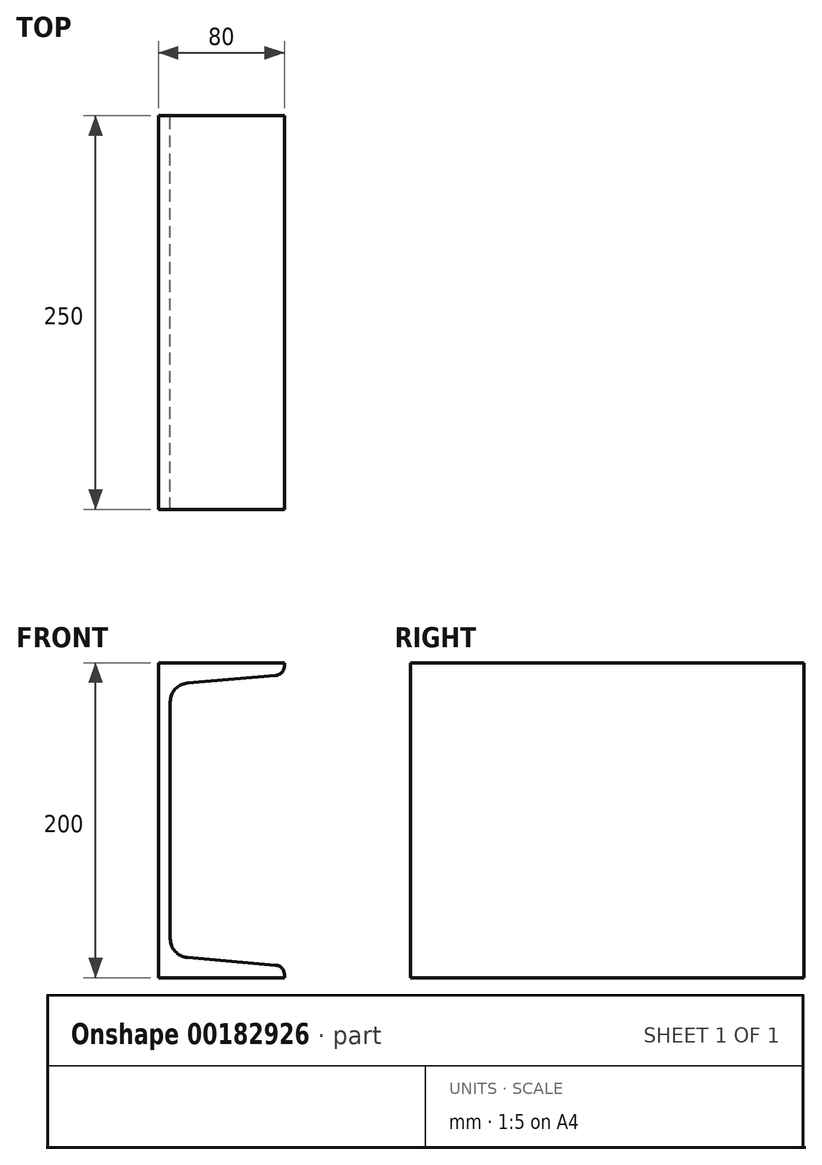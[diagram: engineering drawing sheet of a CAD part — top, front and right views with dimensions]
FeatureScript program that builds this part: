
annotation { "Feature Type Name" : "Feature", "Feature Type Description" : "" }
export const myFeature = defineFeature(function(context is Context, id is Id, definition is map)
    precondition{}
    {
        {
            var Q0;
            Q0=qCreatedBy(makeId("Front.planeOp"),FACE);
            var sketch = newSketch(context, id + "F0", { "sketchPlane" : qUnion([Q0])});
            skLineSegment(sketch, "E0.bottom", {"start": v(0, 0) * mm, "end": v(80, 0) * mm});
            skLineSegment(sketch, "E0.top", {"start": v(0, 100) * mm, "end": v(80, 100) * mm});
            skLineSegment(sketch, "E0.left", {"start": v(0, 0) * mm, "end": v(0, 100) * mm});
            skLineSegment(sketch, "E0.right", {"start": v(80, 98) * mm, "end": v(80, 100) * mm});
            skLineSegment(sketch, "E1.0", {"start": v(7.5, 0) * mm, "end": v(7.5, 75.16) * mm});
            skLineSegment(sketch, "E2", {"start": v(40, 100) * mm, "end": v(40, 89) * mm});
            skLineSegment(sketch, "E3.0", {"start": v(7.5, 89) * mm, "end": v(80, 89) * mm});
            skPoint(sketch, "E4.orphan", {"position": v(40, 0) * mm});
            skLineSegment(sketch, "E5", {"start": v(40, 89) * mm, "end": v(74.52, 92.02) * mm});
            skLineSegment(sketch, "E6", {"start": v(40, 89) * mm, "end": v(18.45, 87.11) * mm});
            skPoint(sketch, "E7.newPointB", {"position": v(80, 0) * mm});
            skArc(sketch, "E7.filletArc", {"start": v(74.52, 92.02) * mm, "mid": v(78.42, 93.94) * mm, "end": v(80, 98) * mm});
            skArc(sketch, "E8.filletArc", {"start": v(18.45, 87.11) * mm, "mid": v(10.65, 83.27) * mm, "end": v(7.5, 75.16) * mm});
            skLineSegment(sketch, "E9.MirrorCS", {"start": v(80, -98) * mm, "end": v(80, -100) * mm});
            skLineSegment(sketch, "E10.MirrorCS", {"start": v(40, -100) * mm, "end": v(40, -89) * mm});
            skArc(sketch, "E11.MirrorCS", {"start": v(74.52, -92.02) * mm, "mid": v(78.42, -93.94) * mm, "end": v(80, -98) * mm});
            skLineSegment(sketch, "E12.MirrorCS", {"start": v(0, -100) * mm, "end": v(80, -100) * mm});
            skLineSegment(sketch, "E13.MirrorCS", {"start": v(7.5, -89) * mm, "end": v(80, -89) * mm});
            skLineSegment(sketch, "E14.MirrorCS", {"start": v(40, -89) * mm, "end": v(74.52, -92.02) * mm});
            skLineSegment(sketch, "E15.MirrorCS", {"start": v(40, -89) * mm, "end": v(18.45, -87.11) * mm});
            skLineSegment(sketch, "E16.MirrorCS", {"start": v(0, 0) * mm, "end": v(0, -100) * mm});
            skArc(sketch, "E17.MirrorCS", {"start": v(18.45, -87.11) * mm, "mid": v(10.65, -83.27) * mm, "end": v(7.5, -75.16) * mm});
            skLineSegment(sketch, "E18.MirrorCS", {"start": v(7.5, 0) * mm, "end": v(7.5, -75.16) * mm});
            skSolve(sketch);
        }
        {
            var Q0;
            {var subQ1=sQuery(id+"F0.wireOp",EDGE,"E0.left");Q0=makeQuery(id+"F0.imprint","IMPRINT",FACE,{"disambiguationData":[TD([[makeQuery(id+"F0.imprint","IMPRINT",EDGE,{"derivedFrom":subQ1}),-1.0]])]});}
            var Q1;
            {var subQ1=sQuery(id+"F0.wireOp",EDGE,"E0.right");Q1=makeQuery(id+"F0.imprint","IMPRINT",FACE,{"disambiguationData":[TD([[makeQuery(id+"F0.imprint","IMPRINT",EDGE,{"derivedFrom":subQ1}),1.0]])]});}
            var Q2;
            {var subQ1=sQuery(id+"F0.wireOp",EDGE,"E10.MirrorCS");Q2=makeQuery(id+"F0.imprint","IMPRINT",FACE,{"disambiguationData":[TD([[makeQuery(id+"F0.imprint","IMPRINT",EDGE,{"derivedFrom":subQ1}),1.0]])]});}
            var Q3;
            {var subQ1=sQuery(id+"F0.wireOp",EDGE,"E9.MirrorCS");Q3=makeQuery(id+"F0.imprint","IMPRINT",FACE,{"disambiguationData":[TD([[makeQuery(id+"F0.imprint","IMPRINT",EDGE,{"derivedFrom":subQ1}),-1.0]])]});}
            extrude(context, id + "F1", {"entities" : qUnion([Q0, Q1, Q2, Q3]), "endBound" : BoundingType.SYMMETRIC, "depth" : 250 * mm});
        }
    });
